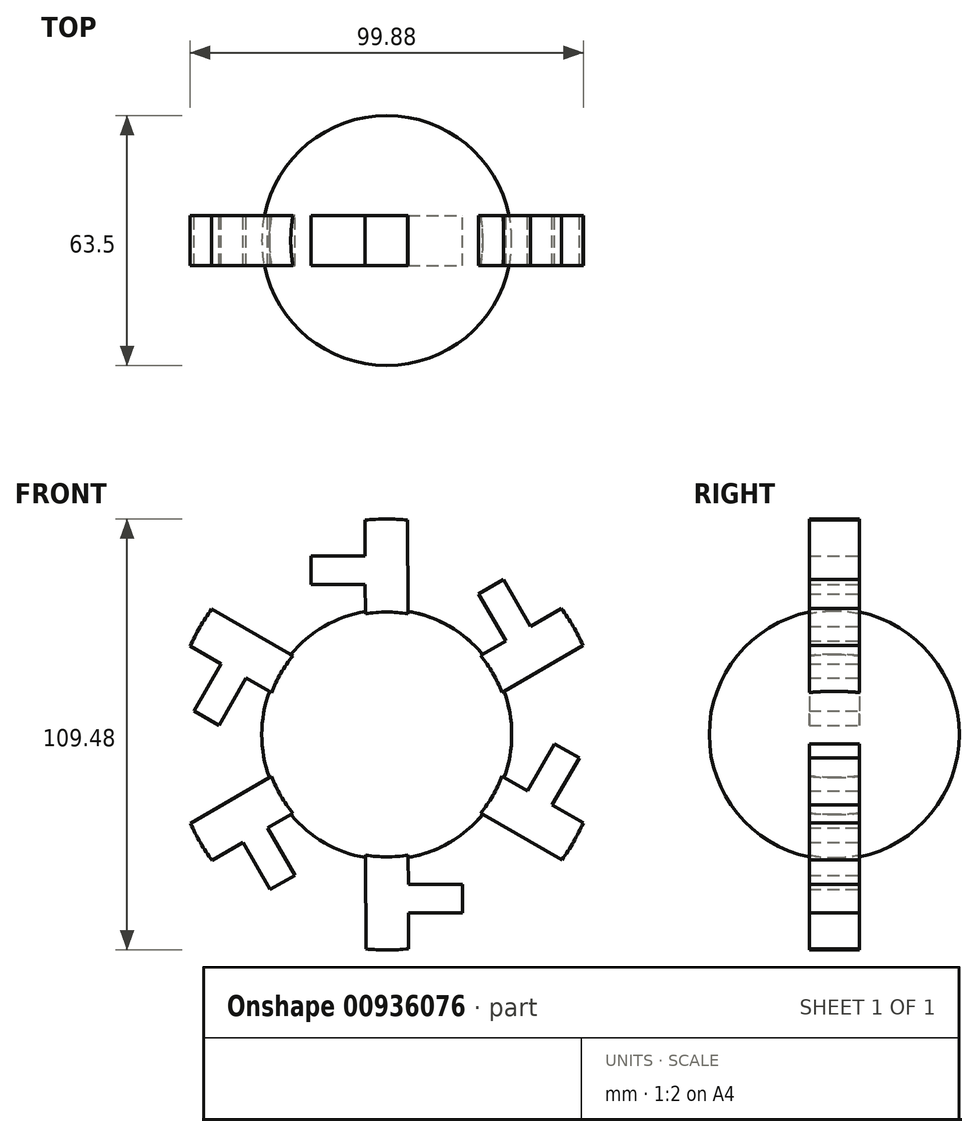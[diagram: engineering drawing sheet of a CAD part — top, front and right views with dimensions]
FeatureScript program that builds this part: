
annotation { "Feature Type Name" : "Feature", "Feature Type Description" : "" }
export const myFeature = defineFeature(function(context is Context, id is Id, definition is map)
    precondition{}
    {
        {
            var Q0;
            Q0=qCreatedBy(makeId("Front.planeOp"),FACE);
            var sketch = newSketch(context, id + "F0", { "sketchPlane" : qUnion([Q0])});
            skArc(sketch, "E0", {"start": v(5.31, 54.48) * mm, "mid": v(-0.12, 54.74) * mm, "end": v(-5.54, 54.46) * mm});
            skCircle(sketch, "E1", {"center": v(0, 0) * mm, "radius": 31.75 * mm});
            skLineSegment(sketch, "E2.left", {"start": v(-5.45, 31.28) * mm, "end": v(-5.48, 38.1) * mm});
            skLineSegment(sketch, "E2.right", {"start": v(5.4, 31.29) * mm, "end": v(5.31, 54.48) * mm});
            skLineSegment(sketch, "E3.bottom", {"start": v(-5.48, 38.1) * mm, "end": v(-19.28, 38.1) * mm});
            skLineSegment(sketch, "E3.top", {"start": v(-5.5, 45.36) * mm, "end": v(-19.28, 45.36) * mm});
            skLineSegment(sketch, "E3.left", {"start": v(5.38, 38.1) * mm, "end": v(5.38, 45.36) * mm});
            skLineSegment(sketch, "E3.right", {"start": v(-19.28, 38.1) * mm, "end": v(-19.28, 45.36) * mm});
            skLineSegment(sketch, "E4.trimOffspring", {"start": v(-5.5, 45.36) * mm, "end": v(-5.54, 54.46) * mm});
            skLineSegment(sketch, "E5.1.0", {"start": v(-30.3, 23.7) * mm, "end": v(-36.6, 27.34) * mm});
            skLineSegment(sketch, "E5.1.1", {"start": v(-24.4, 20.32) * mm, "end": v(-44.53, 31.84) * mm});
            skArc(sketch, "E5.1.2", {"start": v(-44.53, 31.84) * mm, "mid": v(-47.47, 27.27) * mm, "end": v(-49.94, 22.43) * mm});
            skLineSegment(sketch, "E5.1.3", {"start": v(-42.04, 17.9) * mm, "end": v(-49.94, 22.43) * mm});
            skLineSegment(sketch, "E5.1.4", {"start": v(-29.81, 10.92) * mm, "end": v(-35.74, 14.3) * mm});
            skLineSegment(sketch, "E5.1.5", {"start": v(-35.74, 14.3) * mm, "end": v(-42.64, 2.35) * mm});
            skLineSegment(sketch, "E5.1.6", {"start": v(-42.64, 2.35) * mm, "end": v(-48.92, 5.98) * mm});
            skLineSegment(sketch, "E5.1.7", {"start": v(-42.04, 17.9) * mm, "end": v(-48.92, 5.98) * mm});
            skArc(sketch, "E5.2.2", {"start": v(-49.84, -22.64) * mm, "mid": v(-47.35, -27.47) * mm, "end": v(-44.4, -32.03) * mm});
            skLineSegment(sketch, "E5.2.3", {"start": v(-36.53, -27.45) * mm, "end": v(-44.4, -32.03) * mm});
            skLineSegment(sketch, "E5.2.4", {"start": v(-24.36, -20.36) * mm, "end": v(-30.26, -23.8) * mm});
            skLineSegment(sketch, "E5.2.5", {"start": v(-30.26, -23.8) * mm, "end": v(-23.35, -35.75) * mm});
            skLineSegment(sketch, "E5.2.6", {"start": v(-23.35, -35.75) * mm, "end": v(-29.64, -39.38) * mm});
            skLineSegment(sketch, "E5.2.7", {"start": v(-36.53, -27.45) * mm, "end": v(-29.64, -39.38) * mm});
            skLineSegment(sketch, "E5.3.1", {"start": v(-5.4, -31.29) * mm, "end": v(-5.31, -54.48) * mm});
            skArc(sketch, "E5.3.2", {"start": v(-5.31, -54.48) * mm, "mid": v(0.12, -54.74) * mm, "end": v(5.54, -54.46) * mm});
            skLineSegment(sketch, "E5.3.3", {"start": v(5.5, -45.36) * mm, "end": v(5.54, -54.46) * mm});
            skLineSegment(sketch, "E5.3.4", {"start": v(5.45, -31.28) * mm, "end": v(5.48, -38.1) * mm});
            skLineSegment(sketch, "E5.3.5", {"start": v(5.48, -38.1) * mm, "end": v(19.28, -38.1) * mm});
            skLineSegment(sketch, "E5.3.6", {"start": v(19.28, -38.1) * mm, "end": v(19.28, -45.36) * mm});
            skLineSegment(sketch, "E5.3.7", {"start": v(5.5, -45.36) * mm, "end": v(19.28, -45.36) * mm});
            skLineSegment(sketch, "E5.4.0", {"start": v(30.3, -23.7) * mm, "end": v(36.6, -27.34) * mm});
            skLineSegment(sketch, "E5.4.1", {"start": v(24.4, -20.32) * mm, "end": v(44.53, -31.84) * mm});
            skArc(sketch, "E5.4.2", {"start": v(44.53, -31.84) * mm, "mid": v(47.47, -27.27) * mm, "end": v(49.94, -22.43) * mm});
            skLineSegment(sketch, "E5.4.3", {"start": v(42.04, -17.9) * mm, "end": v(49.94, -22.43) * mm});
            skLineSegment(sketch, "E5.4.4", {"start": v(29.81, -10.92) * mm, "end": v(35.74, -14.3) * mm});
            skLineSegment(sketch, "E5.4.5", {"start": v(35.74, -14.3) * mm, "end": v(42.64, -2.35) * mm});
            skLineSegment(sketch, "E5.4.6", {"start": v(42.64, -2.35) * mm, "end": v(48.92, -5.98) * mm});
            skLineSegment(sketch, "E5.4.7", {"start": v(42.04, -17.9) * mm, "end": v(48.92, -5.98) * mm});
            skLineSegment(sketch, "E6.3.5.0", {"start": v(29.8, 10.96) * mm, "end": v(49.84, 22.64) * mm});
            skArc(sketch, "E6.6.5.0", {"start": v(49.84, 22.64) * mm, "mid": v(47.35, 27.47) * mm, "end": v(44.4, 32.03) * mm});
            skLineSegment(sketch, "E6.10.5.0", {"start": v(36.53, 27.45) * mm, "end": v(44.4, 32.03) * mm});
            skLineSegment(sketch, "E6.13.5.0", {"start": v(24.36, 20.36) * mm, "end": v(30.26, 23.8) * mm});
            skLineSegment(sketch, "E6.16.5.0", {"start": v(30.26, 23.8) * mm, "end": v(23.35, 35.75) * mm});
            skLineSegment(sketch, "E6.19.5.0", {"start": v(23.35, 35.75) * mm, "end": v(29.64, 39.38) * mm});
            skLineSegment(sketch, "E6.22.5.0", {"start": v(36.53, 27.45) * mm, "end": v(29.64, 39.38) * mm});
            skLineSegment(sketch, "E7", {"start": v(-49.84, -22.64) * mm, "end": v(-29.8, -10.96) * mm});
            skLineSegment(sketch, "E8", {"start": v(0, 31.75) * mm, "end": v(0, -31.75) * mm});
            skArc(sketch, "E9", {"start": v(0, -31.75) * mm, "mid": v(31.82, 0) * mm, "end": v(0, 31.75) * mm});
            skSolve(sketch);
        }
        {
            var Q0;
            {var subQ0=sQuery(id+"F0.wireOp",EDGE,"E1");var subQ8=makeQuery(id+"F0.imprint","INTERSECT",VERTEX,{"derivedFrom":[subQ0,sQuery(id+"F0.wireOp",EDGE,"E6.3.5.0")]});Q0=makeQuery(id+"F0.imprint","IMPRINT",FACE,{"disambiguationData":[TD([[makeQuery(id+"F0.imprint","IMPRINT",EDGE,{"disambiguationData":[TD([[subQ8,-1.0]])],"derivedFrom":subQ0}),1.0]])]});}
            var Q1;
            Q1=sQuery(id+"F0.wireOp",EDGE,"LUBLXvIy-f66G-DNDe-dyuX-JFYQiY3sf9gK");
            var Q2;
            Q2=sQuery(id+"F0.wireOp",EDGE,"E9");
            var Q3;
            Q3=sQuery(id+"F0.wireOp",EDGE,"E8");
            revolve(context, id + "F1", {"bodyType" : ToolBodyType.SURFACE, "surfaceOperationType" : NewSurfaceOperationType.NEW, "entities" : qUnion([Q0]), "surfaceEntities" : qUnion([Q1, Q2]), "axis" : qUnion([Q3]), "revolveType" : RevolveType.FULL});
        }
        {
            var Q0;
            {var subQ2=sQuery(id+"F0.wireOp",EDGE,"E8");Q0=makeQuery(id+"F0.imprint","IMPRINT",FACE,{"disambiguationData":[TD([[makeQuery(id+"F0.imprint","IMPRINT",EDGE,{"derivedFrom":subQ2}),1.0]])]});}
            var Q1;
            Q1=sQuery(id+"F0.wireOp",EDGE,"E8");
            revolve(context, id + "F2", {"surfaceOperationType" : NewSurfaceOperationType.NEW, "entities" : qUnion([Q0]), "axis" : qUnion([Q1]), "revolveType" : RevolveType.FULL});
        }
        {
            var Q0;
            Q0=qCreatedBy(makeId("Front.planeOp"),FACE);
            var sketch = newSketch(context, id + "F3", { "sketchPlane" : qUnion([Q0])});
            skArc(sketch, "E10", {"start": v(5.31, 54.48) * mm, "mid": v(-0.12, 54.74) * mm, "end": v(-5.54, 54.46) * mm});
            skLineSegment(sketch, "E11.left", {"start": v(-5.45, 31.28) * mm, "end": v(-5.48, 38.1) * mm});
            skLineSegment(sketch, "E11.right", {"start": v(5.4, 31.29) * mm, "end": v(5.31, 54.48) * mm});
            skLineSegment(sketch, "E12.bottom", {"start": v(-5.48, 38.1) * mm, "end": v(-19.28, 38.1) * mm});
            skLineSegment(sketch, "E12.top", {"start": v(-5.5, 45.36) * mm, "end": v(-19.28, 45.36) * mm});
            skLineSegment(sketch, "E12.left", {"start": v(5.38, 38.1) * mm, "end": v(5.38, 45.36) * mm});
            skLineSegment(sketch, "E12.right", {"start": v(-19.28, 38.1) * mm, "end": v(-19.28, 45.36) * mm});
            skLineSegment(sketch, "E13.trimOffspring", {"start": v(-5.5, 45.36) * mm, "end": v(-5.54, 54.46) * mm});
            skLineSegment(sketch, "E14.1.0", {"start": v(-30.3, 23.7) * mm, "end": v(-36.6, 27.34) * mm});
            skLineSegment(sketch, "E14.1.1", {"start": v(-24.4, 20.32) * mm, "end": v(-44.53, 31.84) * mm});
            skArc(sketch, "E14.1.2", {"start": v(-44.53, 31.84) * mm, "mid": v(-47.47, 27.27) * mm, "end": v(-49.94, 22.43) * mm});
            skLineSegment(sketch, "E14.1.3", {"start": v(-42.04, 17.9) * mm, "end": v(-49.94, 22.43) * mm});
            skLineSegment(sketch, "E14.1.4", {"start": v(-29.81, 10.92) * mm, "end": v(-35.74, 14.3) * mm});
            skLineSegment(sketch, "E14.1.5", {"start": v(-35.74, 14.3) * mm, "end": v(-42.64, 2.35) * mm});
            skLineSegment(sketch, "E14.1.6", {"start": v(-42.64, 2.35) * mm, "end": v(-48.92, 5.98) * mm});
            skLineSegment(sketch, "E14.1.7", {"start": v(-42.04, 17.9) * mm, "end": v(-48.92, 5.98) * mm});
            skArc(sketch, "E14.2.2", {"start": v(-49.84, -22.64) * mm, "mid": v(-47.35, -27.47) * mm, "end": v(-44.4, -32.03) * mm});
            skLineSegment(sketch, "E14.2.3", {"start": v(-36.53, -27.45) * mm, "end": v(-44.4, -32.03) * mm});
            skLineSegment(sketch, "E14.2.4", {"start": v(-24.36, -20.36) * mm, "end": v(-30.26, -23.8) * mm});
            skLineSegment(sketch, "E14.2.5", {"start": v(-30.26, -23.8) * mm, "end": v(-23.35, -35.75) * mm});
            skLineSegment(sketch, "E14.2.6", {"start": v(-23.35, -35.75) * mm, "end": v(-29.64, -39.38) * mm});
            skLineSegment(sketch, "E14.2.7", {"start": v(-36.53, -27.45) * mm, "end": v(-29.64, -39.38) * mm});
            skLineSegment(sketch, "E14.3.1", {"start": v(-5.4, -31.29) * mm, "end": v(-5.31, -54.48) * mm});
            skArc(sketch, "E14.3.2", {"start": v(-5.31, -54.48) * mm, "mid": v(0.12, -54.74) * mm, "end": v(5.54, -54.46) * mm});
            skLineSegment(sketch, "E14.3.3", {"start": v(5.5, -45.36) * mm, "end": v(5.54, -54.46) * mm});
            skLineSegment(sketch, "E14.3.4", {"start": v(5.45, -31.28) * mm, "end": v(5.48, -38.1) * mm});
            skLineSegment(sketch, "E14.3.5", {"start": v(5.48, -38.1) * mm, "end": v(19.28, -38.1) * mm});
            skLineSegment(sketch, "E14.3.6", {"start": v(19.28, -38.1) * mm, "end": v(19.28, -45.36) * mm});
            skLineSegment(sketch, "E14.3.7", {"start": v(5.5, -45.36) * mm, "end": v(19.28, -45.36) * mm});
            skLineSegment(sketch, "E14.4.0", {"start": v(30.3, -23.7) * mm, "end": v(36.6, -27.34) * mm});
            skLineSegment(sketch, "E14.4.1", {"start": v(24.4, -20.32) * mm, "end": v(44.53, -31.84) * mm});
            skArc(sketch, "E14.4.2", {"start": v(44.53, -31.84) * mm, "mid": v(47.47, -27.27) * mm, "end": v(49.94, -22.43) * mm});
            skLineSegment(sketch, "E14.4.3", {"start": v(42.04, -17.9) * mm, "end": v(49.94, -22.43) * mm});
            skLineSegment(sketch, "E14.4.4", {"start": v(29.81, -10.92) * mm, "end": v(35.74, -14.3) * mm});
            skLineSegment(sketch, "E14.4.5", {"start": v(35.74, -14.3) * mm, "end": v(42.64, -2.35) * mm});
            skLineSegment(sketch, "E14.4.6", {"start": v(42.64, -2.35) * mm, "end": v(48.92, -5.98) * mm});
            skLineSegment(sketch, "E14.4.7", {"start": v(42.04, -17.9) * mm, "end": v(48.92, -5.98) * mm});
            skLineSegment(sketch, "E15.3.5.0", {"start": v(29.8, 10.96) * mm, "end": v(49.84, 22.64) * mm});
            skArc(sketch, "E15.6.5.0", {"start": v(49.84, 22.64) * mm, "mid": v(47.35, 27.47) * mm, "end": v(44.4, 32.03) * mm});
            skLineSegment(sketch, "E15.10.5.0", {"start": v(36.53, 27.45) * mm, "end": v(44.4, 32.03) * mm});
            skLineSegment(sketch, "E15.13.5.0", {"start": v(24.36, 20.36) * mm, "end": v(30.26, 23.8) * mm});
            skLineSegment(sketch, "E15.16.5.0", {"start": v(30.26, 23.8) * mm, "end": v(23.35, 35.75) * mm});
            skLineSegment(sketch, "E15.19.5.0", {"start": v(23.35, 35.75) * mm, "end": v(29.64, 39.38) * mm});
            skLineSegment(sketch, "E15.22.5.0", {"start": v(36.53, 27.45) * mm, "end": v(29.64, 39.38) * mm});
            skLineSegment(sketch, "E16", {"start": v(-49.84, -22.64) * mm, "end": v(-29.8, -10.96) * mm});
            skLineSegment(sketch, "E17", {"start": v(-5.45, 31.28) * mm, "end": v(-5.45, 22.39) * mm});
            skLineSegment(sketch, "E18", {"start": v(-5.45, 22.39) * mm, "end": v(5.4, 22.39) * mm});
            skLineSegment(sketch, "E19", {"start": v(5.4, 22.39) * mm, "end": v(5.4, 31.29) * mm});
            skLineSegment(sketch, "E20.1.0", {"start": v(-16.69, 15.87) * mm, "end": v(-24.4, 20.32) * mm});
            skLineSegment(sketch, "E20.1.1", {"start": v(-22.12, 6.47) * mm, "end": v(-16.69, 15.87) * mm});
            skLineSegment(sketch, "E20.1.2", {"start": v(-29.81, 10.92) * mm, "end": v(-22.12, 6.47) * mm});
            skLineSegment(sketch, "E20.2.0", {"start": v(-22.1, -6.51) * mm, "end": v(-29.8, -10.96) * mm});
            skLineSegment(sketch, "E20.2.1", {"start": v(-16.66, -15.92) * mm, "end": v(-22.1, -6.51) * mm});
            skLineSegment(sketch, "E20.2.2", {"start": v(-24.36, -20.36) * mm, "end": v(-16.66, -15.92) * mm});
            skLineSegment(sketch, "E20.3.0", {"start": v(-5.4, -22.39) * mm, "end": v(-5.4, -31.29) * mm});
            skLineSegment(sketch, "E20.3.1", {"start": v(5.45, -22.39) * mm, "end": v(-5.4, -22.39) * mm});
            skLineSegment(sketch, "E20.3.2", {"start": v(5.45, -31.28) * mm, "end": v(5.45, -22.39) * mm});
            skLineSegment(sketch, "E20.4.0", {"start": v(16.69, -15.87) * mm, "end": v(24.4, -20.32) * mm});
            skLineSegment(sketch, "E20.4.1", {"start": v(22.12, -6.47) * mm, "end": v(16.69, -15.87) * mm});
            skLineSegment(sketch, "E20.4.2", {"start": v(29.81, -10.92) * mm, "end": v(22.12, -6.47) * mm});
            skLineSegment(sketch, "E20.5.0", {"start": v(22.1, 6.51) * mm, "end": v(29.8, 10.96) * mm});
            skLineSegment(sketch, "E20.5.1", {"start": v(16.66, 15.92) * mm, "end": v(22.1, 6.51) * mm});
            skLineSegment(sketch, "E20.5.2", {"start": v(24.36, 20.36) * mm, "end": v(16.66, 15.92) * mm});
            skSolve(sketch);
        }
        {
            var Q0;
            {var subQ0=sQuery(id+"F3.wireOp",EDGE,"E10");Q0=makeQuery(id+"F3.imprint","IMPRINT",FACE,{"disambiguationData":[TD([[makeQuery(id+"F3.imprint","IMPRINT",EDGE,{"derivedFrom":subQ0}),1.0]])]});}
            var Q1;
            Q1=makeQuery(id+"F3.imprint","IMPRINT",FACE,{"disambiguationData":[TD([[makeQuery(id+"F3.imprint","IMPRINT",EDGE,{"derivedFrom":sQuery(id+"F3.wireOp",EDGE,"E15.3.5.0")}),1.0]])]});
            var Q2;
            {var subQ3=sQuery(id+"F3.wireOp",EDGE,"E14.4.2");Q2=makeQuery(id+"F3.imprint","IMPRINT",FACE,{"disambiguationData":[TD([[makeQuery(id+"F3.imprint","IMPRINT",EDGE,{"derivedFrom":subQ3}),1.0]])]});}
            var Q3;
            Q3=makeQuery(id+"F3.imprint","IMPRINT",FACE,{"disambiguationData":[TD([[makeQuery(id+"F3.imprint","IMPRINT",EDGE,{"derivedFrom":sQuery(id+"F3.wireOp",EDGE,"E14.3.1")}),1.0]])]});
            var Q4;
            Q4=makeQuery(id+"F3.imprint","IMPRINT",FACE,{"disambiguationData":[TD([[makeQuery(id+"F3.imprint","IMPRINT",EDGE,{"derivedFrom":sQuery(id+"F3.wireOp",EDGE,"E14.2.2")}),1.0]])]});
            var Q5;
            {var subQ3=sQuery(id+"F3.wireOp",EDGE,"E14.1.2");Q5=makeQuery(id+"F3.imprint","IMPRINT",FACE,{"disambiguationData":[TD([[makeQuery(id+"F3.imprint","IMPRINT",EDGE,{"derivedFrom":subQ3}),1.0]])]});}
            extrude(context, id + "F4", {"entities" : qUnion([Q0, Q1, Q2, Q3, Q4, Q5]), "operationType" : NewBodyOperationType.ADD, "endBound" : BoundingType.SYMMETRIC, "depth" : 12.7 * mm, "offsetDistance" : 25.4 * mm});
        }
    });
